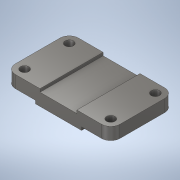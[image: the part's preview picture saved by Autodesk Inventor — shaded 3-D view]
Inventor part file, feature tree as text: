
AUTODESK INVENTOR PART (.ipt)
format: ipt  version: 2020 (Build 240168000, 168)  size: 207,872 bytes
history: native  units: mm
features: extrude x3, sketch x2, fillet x2, mirror x1
ambient origin geometry x8: Origin, YZ Plane, XZ Plane, XY Plane, X Axis, Y Axis, Z Axis, Center Point
bodies: Solid1 (feature_tree)
feature tree (8):
  extrude  "Extrusion1"  Depth=4.0mm
  sketch  "Sketch2"  dims[d2=38.0mm d3=16.0mm d4=44.0mm d5=4.0mm d6=82.0mm d7=0.0mm d8=11.0mm d9=11.0mm d10=12.0mm d11=12.0mm d12=12.0mm d13=12.0mm d14=82.0mm d15=0.0mm d16=82.0mm d17=0.0mm d18=12.0mm d19=12.0mm]
  extrude  "Extrusion2"  Depth=16.0mm
  extrude  "Extrusion3"  Depth=44.0mm
  fillet  "Fillet1"  Radius=4.0mm
  fillet  "Fillet2"  Radius=82.0mm
  mirror  "Mirror1"
  sketch  "Sketch1"  dims[d0=30.0mm d1=4.0mm]
